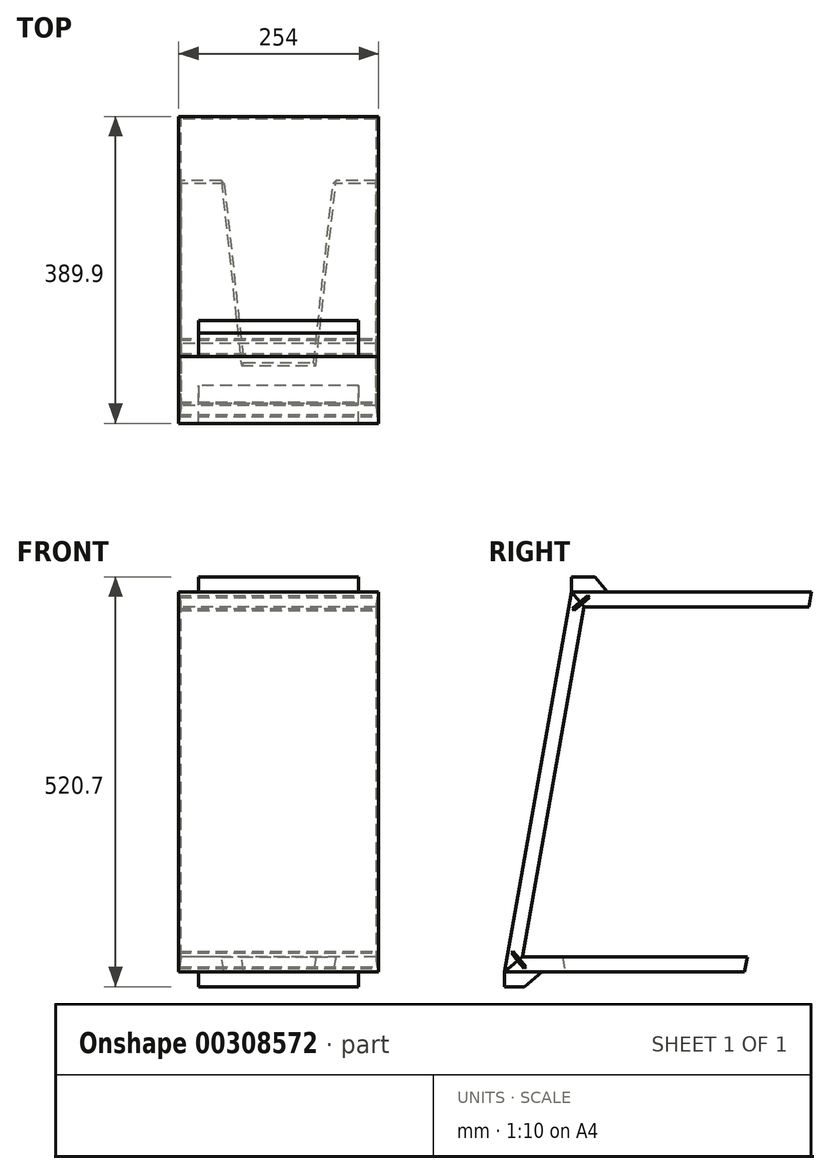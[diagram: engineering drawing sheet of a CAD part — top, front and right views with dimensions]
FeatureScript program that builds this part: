
annotation { "Feature Type Name" : "Feature", "Feature Type Description" : "" }
export const myFeature = defineFeature(function(context is Context, id is Id, definition is map)
    precondition{}
    {
        {
            var Q0;
            Q0=qCreatedBy(makeId("Right.planeOp"),FACE);
            var sketch = newSketch(context, id + "F0", { "sketchPlane" : qUnion([Q0])});
            skLineSegment(sketch, "E0", {"start": v(0, 0) * mm, "end": v(85.1, 482.6) * mm});
            skLineSegment(sketch, "E1", {"start": v(85.1, 482.6) * mm, "end": v(389.9, 482.6) * mm});
            skLineSegment(sketch, "E2", {"start": v(0, 0) * mm, "end": v(304.8, 0) * mm});
            skLineSegment(sketch, "E3", {"start": v(389.9, 482.6) * mm, "end": v(386.54, 463.55) * mm});
            skLineSegment(sketch, "E4", {"start": v(386.54, 463.55) * mm, "end": v(101.08, 463.55) * mm});
            skLineSegment(sketch, "E5", {"start": v(101.08, 463.55) * mm, "end": v(22.7, 19.05) * mm});
            skLineSegment(sketch, "E6", {"start": v(22.7, 19.05) * mm, "end": v(308.16, 19.05) * mm});
            skLineSegment(sketch, "E7", {"start": v(308.16, 19.05) * mm, "end": v(304.8, 0) * mm});
            skLineSegment(sketch, "E8", {"start": v(85.1, 482.6) * mm, "end": v(101.08, 463.55) * mm});
            skLineSegment(sketch, "E9", {"start": v(22.7, 19.05) * mm, "end": v(0, 0) * mm});
            skSolve(sketch);
        }
        {
            var Q0;
            Q0 = qSketchRegion(id + "F0", true);
            extrude(context, id + "F1", {"entities" : qUnion([Q0]), "endBound" : BoundingType.SYMMETRIC, "depth" : 254 * mm, "offsetDistance" : 25.4 * mm});
        }
        {
            var Q0;
            Q0=makeQuery(id+"F1.opExtrude","CAP_EDGE",EDGE,{"disambiguationData":[OSD([sQuery(id+"F0.wireOp",EDGE,"E4")])],"isStart":false});
            var Q1;
            Q1=makeQuery(id+"F1.opExtrude","CAP_EDGE",EDGE,{"disambiguationData":[OSD([sQuery(id+"F0.wireOp",EDGE,"E5")])],"isStart":false});
            var Q2;
            Q2=makeQuery(id+"F1.opExtrude","CAP_EDGE",EDGE,{"disambiguationData":[OSD([sQuery(id+"F0.wireOp",EDGE,"E6")])],"isStart":false});
            chamfer(context, id + "F2", {"entities" : qUnion([Q0, Q1, Q2]), "chamferType" : ChamferType.OFFSET_ANGLE, "width" : 19.05 * mm, "oppositeDirection" : true, "angle" : 10 * degree, "tangentPropagation" : true});
        }
        {
            var Q0;
            Q0=makeQuery(id+"F1.opExtrude","CAP_EDGE",EDGE,{"disambiguationData":[OSD([sQuery(id+"F0.wireOp",EDGE,"E4")])],"isStart":true});
            var Q1;
            Q1=makeQuery(id+"F1.opExtrude","CAP_EDGE",EDGE,{"disambiguationData":[OSD([sQuery(id+"F0.wireOp",EDGE,"E5")])],"isStart":true});
            var Q2;
            Q2=makeQuery(id+"F1.opExtrude","CAP_EDGE",EDGE,{"disambiguationData":[OSD([sQuery(id+"F0.wireOp",EDGE,"E6")])],"isStart":true});
            chamfer(context, id + "F3", {"entities" : qUnion([Q0, Q1, Q2]), "chamferType" : ChamferType.OFFSET_ANGLE, "width" : 19.05 * mm, "oppositeDirection" : false, "angle" : 10 * degree, "tangentPropagation" : true});
        }
        {
            var Q0;
            Q0=makeQuery(id+"F1.opExtrude","SWEPT_FACE",FACE,{"disambiguationData":[OSD([sQuery(id+"F0.wireOp",EDGE,"E6")])]});
            var sketch = newSketch(context, id + "F4", { "sketchPlane" : qUnion([Q0])});
            skLineSegment(sketch, "E10", {"start": v(0, 22.7) * mm, "end": v(0, 308.16) * mm, "construction": true});
            skLineSegment(sketch, "E11", {"start": v(72.84, 308.16) * mm, "end": v(47.44, 73.5) * mm});
            skLineSegment(sketch, "E12", {"start": v(47.44, 73.5) * mm, "end": v(0, 73.5) * mm});
            skLineSegment(sketch, "E13", {"start": v(72.84, 308.16) * mm, "end": v(0, 308.16) * mm});
            skLineSegment(sketch, "E14", {"start": v(0, 308.16) * mm, "end": v(-72.84, 308.16) * mm});
            skLineSegment(sketch, "E15", {"start": v(-72.84, 308.16) * mm, "end": v(-47.44, 73.5) * mm});
            skLineSegment(sketch, "E16", {"start": v(-47.44, 73.5) * mm, "end": v(0, 73.5) * mm});
            skSolve(sketch);
        }
        {
            var Q0;
            Q0 = qSketchRegion(id + "F4", true);
            extrude(context, id + "F5", {"entities" : qUnion([Q0]), "operationType" : NewBodyOperationType.REMOVE, "endBound" : BoundingType.THROUGH_ALL, "oppositeDirection" : true, "depth" : 25.4 * mm, "offsetDistance" : 25.4 * mm, "hasDraft" : true, "draftAngle" : 10 * degree, "draftPullDirection" : true});
        }
        {
            var Q0;
            Q0=qCreatedBy(makeId("Right.planeOp"),FACE);
            var sketch = newSketch(context, id + "F6", { "sketchPlane" : qUnion([Q0])});
            skLineSegment(sketch, "E17.0", {"start": v(101.08, 463.55) * mm, "end": v(85.1, 482.6) * mm, "construction": true});
            skLineSegment(sketch, "E18.bottom", {"start": v(88.3, 459.03) * mm, "end": v(107.75, 475.36) * mm});
            skLineSegment(sketch, "E18.top", {"start": v(86.25, 461.47) * mm, "end": v(105.7, 477.8) * mm});
            skLineSegment(sketch, "E18.left", {"start": v(88.3, 459.03) * mm, "end": v(86.25, 461.47) * mm});
            skLineSegment(sketch, "E18.right", {"start": v(107.75, 475.36) * mm, "end": v(105.7, 477.8) * mm});
            skLineSegment(sketch, "E19.0", {"start": v(22.7, 19.05) * mm, "end": v(0, 0) * mm, "construction": true});
            skLineSegment(sketch, "E20.bottom", {"start": v(10.9, 25.72) * mm, "end": v(27.22, 6.26) * mm});
            skLineSegment(sketch, "E20.top", {"start": v(8.46, 23.68) * mm, "end": v(24.79, 4.22) * mm});
            skLineSegment(sketch, "E20.left", {"start": v(10.9, 25.72) * mm, "end": v(8.46, 23.68) * mm});
            skLineSegment(sketch, "E20.right", {"start": v(27.22, 6.26) * mm, "end": v(24.79, 4.22) * mm});
            skSolve(sketch);
        }
        {
            var Q0;
            Q0 = qSketchRegion(id + "F6", true);
            extrude(context, id + "F7", {"entities" : qUnion([Q0]), "operationType" : NewBodyOperationType.REMOVE, "endBound" : BoundingType.THROUGH_ALL, "oppositeDirection" : true, "depth" : 25.4 * mm, "offsetDistance" : 25.4 * mm, "hasSecondDirection" : true, "secondDirectionBound" : SecondDirectionBoundingType.THROUGH_ALL, "secondDirectionOppositeDirection" : false, "secondDirectionDepth" : 25.4 * mm});
        }
        {
            var Q0;
            Q0=qCreatedBy(makeId("Right.planeOp"),FACE);
            var sketch = newSketch(context, id + "F8", { "sketchPlane" : qUnion([Q0])});
            skLineSegment(sketch, "E21.bottom", {"start": v(85.1, 501.65) * mm, "end": v(114.8, 501.65) * mm});
            skLineSegment(sketch, "E21.top", {"start": v(85.1, 482.6) * mm, "end": v(130.78, 482.6) * mm});
            skLineSegment(sketch, "E21.left", {"start": v(85.1, 501.65) * mm, "end": v(85.1, 482.6) * mm});
            skLineSegment(sketch, "E22", {"start": v(130.78, 482.6) * mm, "end": v(114.8, 501.65) * mm});
            skLineSegment(sketch, "E23", {"start": v(122.79, 492.13) * mm, "end": v(105.7, 477.8) * mm, "construction": true});
            skLineSegment(sketch, "E24.bottom", {"start": v(0, 0) * mm, "end": v(47.67, 0) * mm});
            skLineSegment(sketch, "E24.top", {"start": v(0, -19.05) * mm, "end": v(24.97, -19.05) * mm});
            skLineSegment(sketch, "E24.left", {"start": v(0, 0) * mm, "end": v(0, -19.05) * mm});
            skLineSegment(sketch, "E24.right", {"start": v(47.67, 0) * mm, "end": v(24.97, -19.05) * mm});
            skLineSegment(sketch, "E25", {"start": v(36.32, -9.52) * mm, "end": v(24.79, 4.22) * mm, "construction": true});
            skSolve(sketch);
        }
        {
            var Q0;
            Q0 = qSketchRegion(id + "F8", true);
            extrude(context, id + "F9", {"entities" : qUnion([Q0]), "endBound" : BoundingType.SYMMETRIC, "depth" : 203.2 * mm, "offsetDistance" : 25.4 * mm});
        }
    });
